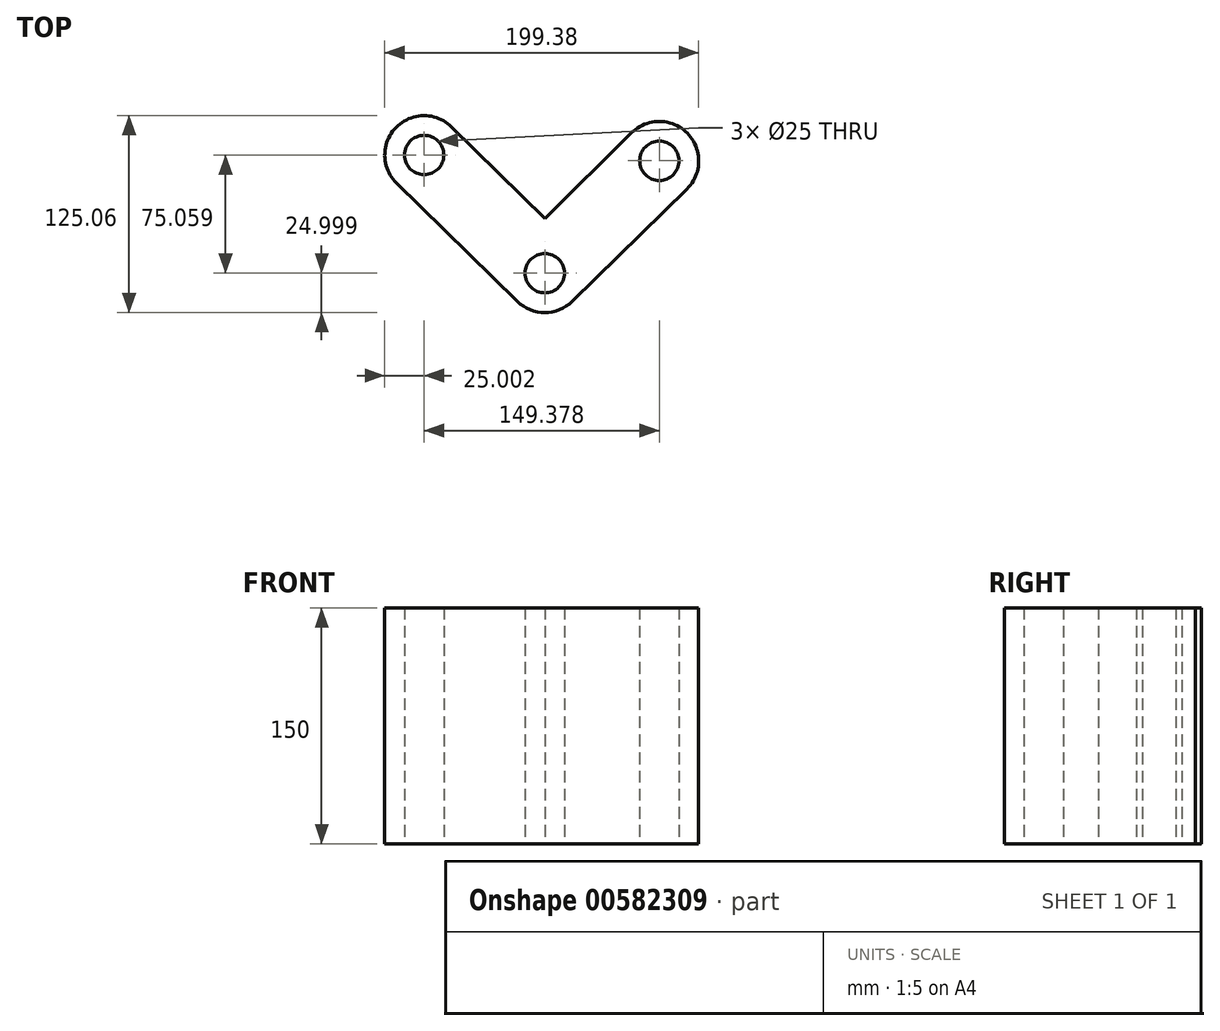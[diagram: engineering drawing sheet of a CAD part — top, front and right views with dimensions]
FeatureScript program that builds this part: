
annotation { "Feature Type Name" : "Feature", "Feature Type Description" : "" }
export const myFeature = defineFeature(function(context is Context, id is Id, definition is map)
    precondition{}
    {
        {
            var Q0;
            Q0=qCreatedBy(makeId("Top.planeOp"),FACE);
            var sketch = newSketch(context, id + "F0", { "sketchPlane" : qUnion([Q0])});
            skCircle(sketch, "E0", {"center": v(-68.17, 21.54) * mm, "radius": 12.5 * mm});
            skArc(sketch, "E1", {"start": v(-50.67, 39.4) * mm, "mid": v(-86.03, 39.03) * mm, "end": v(-85.66, 3.68) * mm});
            skCircle(sketch, "E2", {"center": v(81.2, 17.85) * mm, "radius": 12.5 * mm});
            skArc(sketch, "E3", {"start": v(98.72, 0) * mm, "mid": v(99.02, 35.4) * mm, "end": v(63.63, 35.62) * mm});
            skCircle(sketch, "E4", {"center": v(8.46, -53.52) * mm, "radius": 12.5 * mm});
            skArc(sketch, "E5", {"start": v(-9.03, -71.38) * mm, "mid": v(8.47, -78.52) * mm, "end": v(25.97, -71.37) * mm});
            skLineSegment(sketch, "E6", {"start": v(98.72, 0) * mm, "end": v(25.97, -71.37) * mm});
            skLineSegment(sketch, "E7", {"start": v(-85.66, 3.68) * mm, "end": v(-9.03, -71.38) * mm});
            skLineSegment(sketch, "E8", {"start": v(63.63, 35.62) * mm, "end": v(8.68, -18.74) * mm});
            skLineSegment(sketch, "E9", {"start": v(-50.67, 39.4) * mm, "end": v(8.68, -18.74) * mm});
            skSolve(sketch);
        }
        {
            var Q0;
            Q0=makeQuery(id+"F0.imprint","IMPRINT",FACE,{"disambiguationData":[TD([[makeQuery(id+"F0.imprint","IMPRINT",EDGE,{"derivedFrom":sQuery(id+"F0.wireOp",EDGE,"E2")}),-1.0]])]});
            var Q1;
            Q1=makeQuery(id+"F0.imprint","IMPRINT",FACE,{"disambiguationData":[TD([[makeQuery(id+"F0.imprint","IMPRINT",EDGE,{"derivedFrom":sQuery(id+"F0.wireOp",EDGE,"E4")}),-1.0]])]});
            var Q2;
            Q2=makeQuery(id+"F0.imprint","IMPRINT",FACE,{"disambiguationData":[TD([[makeQuery(id+"F0.imprint","IMPRINT",EDGE,{"derivedFrom":sQuery(id+"F0.wireOp",EDGE,"E0")}),-1.0]])]});
            extrude(context, id + "F1", {"entities" : qUnion([Q0, Q1, Q2]), "depth" : 150 * mm, "offsetDistance" : 25.4 * mm});
        }
        {
            var Q0;
            Q0=sQuery(id+"F0.wireOp",EDGE,"E8");
            var Q1;
            Q1=sQuery(id+"F0.wireOp",EDGE,"E6");
            extrude(context, id + "F2", {"bodyType" : ToolBodyType.SURFACE, "surfaceEntities" : qUnion([Q0, Q1]), "depth" : 50 * mm, "offsetDistance" : 25.4 * mm});
        }
        {
            var Q0;
            Q0=makeQuery(id+"F0.imprint","IMPRINT",FACE,{"disambiguationData":[TD([[makeQuery(id+"F0.imprint","IMPRINT",EDGE,{"derivedFrom":sQuery(id+"F0.wireOp",EDGE,"E0")}),-1.0]])]});
            extrude(context, id + "F3", {"entities" : qUnion([Q0]), "operationType" : NewBodyOperationType.ADD, "depth" : 50 * mm, "offsetDistance" : 25.4 * mm});
        }
    });
